# Revit family: Construction_Roof-Accessories_TRA-Snow-Sun_Snow-Bracket-A-Apex
name_source: partatom
category: Specialty Equipment
units: mm (PartAtom-declared; Revit-internal decimal feet)

## family parameters
Classification Number = 23.35.20.31.27.14
Cut with Voids When Loaded = No
Enable Cutting in Views = No
Host = Face
Maintain Annotation Orientation = No
Part Type = Normal
Room Calculation Point = No
Round Connector Dimension = Use Diameter
Shared = No

## types (1)
- Snow Bracket A Apex
    Default Elevation = 48 "
    Description = Snow Bracket A Apex - Used on: New construction concrete tiles which are installed using horizontal battens. Specifically – Eagle, Boral, Hanson, and other similar tiles
    Height = 3.74 "
    Installation Offset = 0 "
    Length = 16.27 "
    Manufacturer = TRA Snow & Sun
    Model = Snow Bracket A Apex
    Product Documentation Link = https://trasnowandsun.com
    Product Page URL = https://trasnowandsun.com
    Product data url = https://bimobject.com
    URL = https://trasnowandsun.com
    Version = 1
    Weight = 0.63 lbf
    Width = 2.25 "
    z_Installation Offset = 0 "

## geometry (parser evidence)
native form markers: Sweep x4
no freeform markers — native parametric forms only
